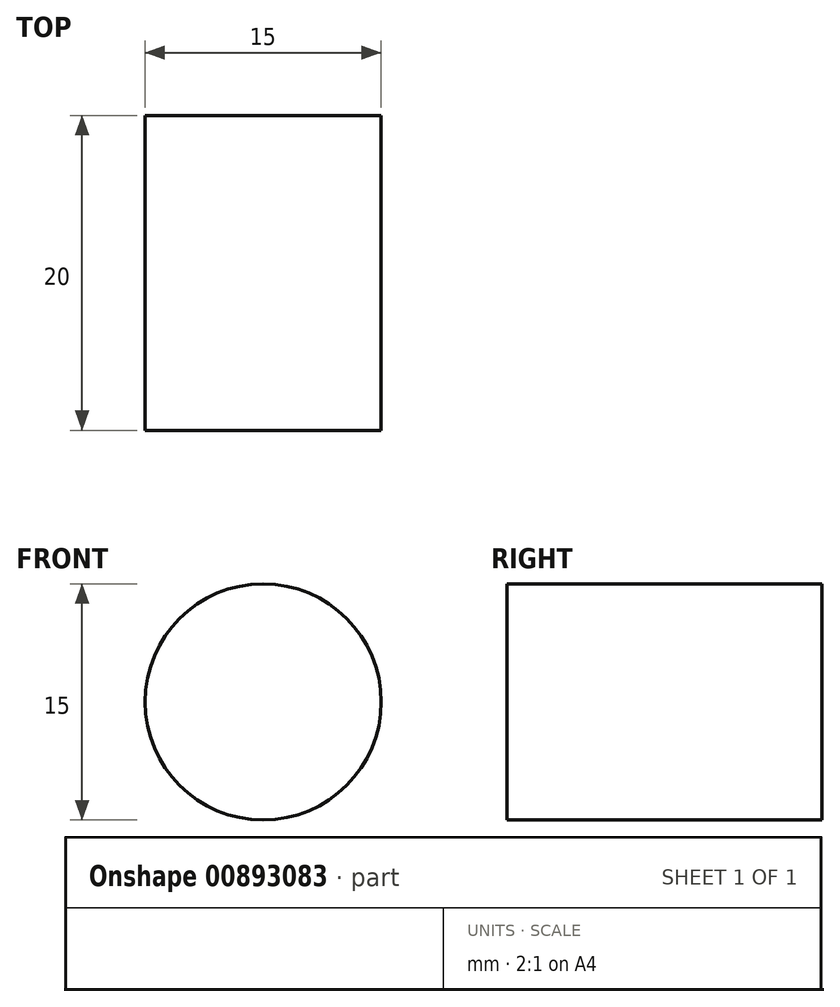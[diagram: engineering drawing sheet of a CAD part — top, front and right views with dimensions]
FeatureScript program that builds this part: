
annotation { "Feature Type Name" : "Feature", "Feature Type Description" : "" }
export const myFeature = defineFeature(function(context is Context, id is Id, definition is map)
    precondition{}
    {
        {
            var Q0;
            Q0=qCreatedBy(makeId("Front.planeOp"),FACE);
            var sketch = newSketch(context, id + "F0", { "sketchPlane" : qUnion([Q0])});
            skCircle(sketch, "E0", {"center": v(0, 0) * mm, "radius": 7.5 * mm});
            skSolve(sketch);
        }
        {
            var Q0;
            Q0 = qSketchRegion(id + "F0", true);
            extrude(context, id + "F1", {"entities" : qUnion([Q0]), "depth" : 20 * mm, "offsetDistance" : 25 * mm});
        }
    });
